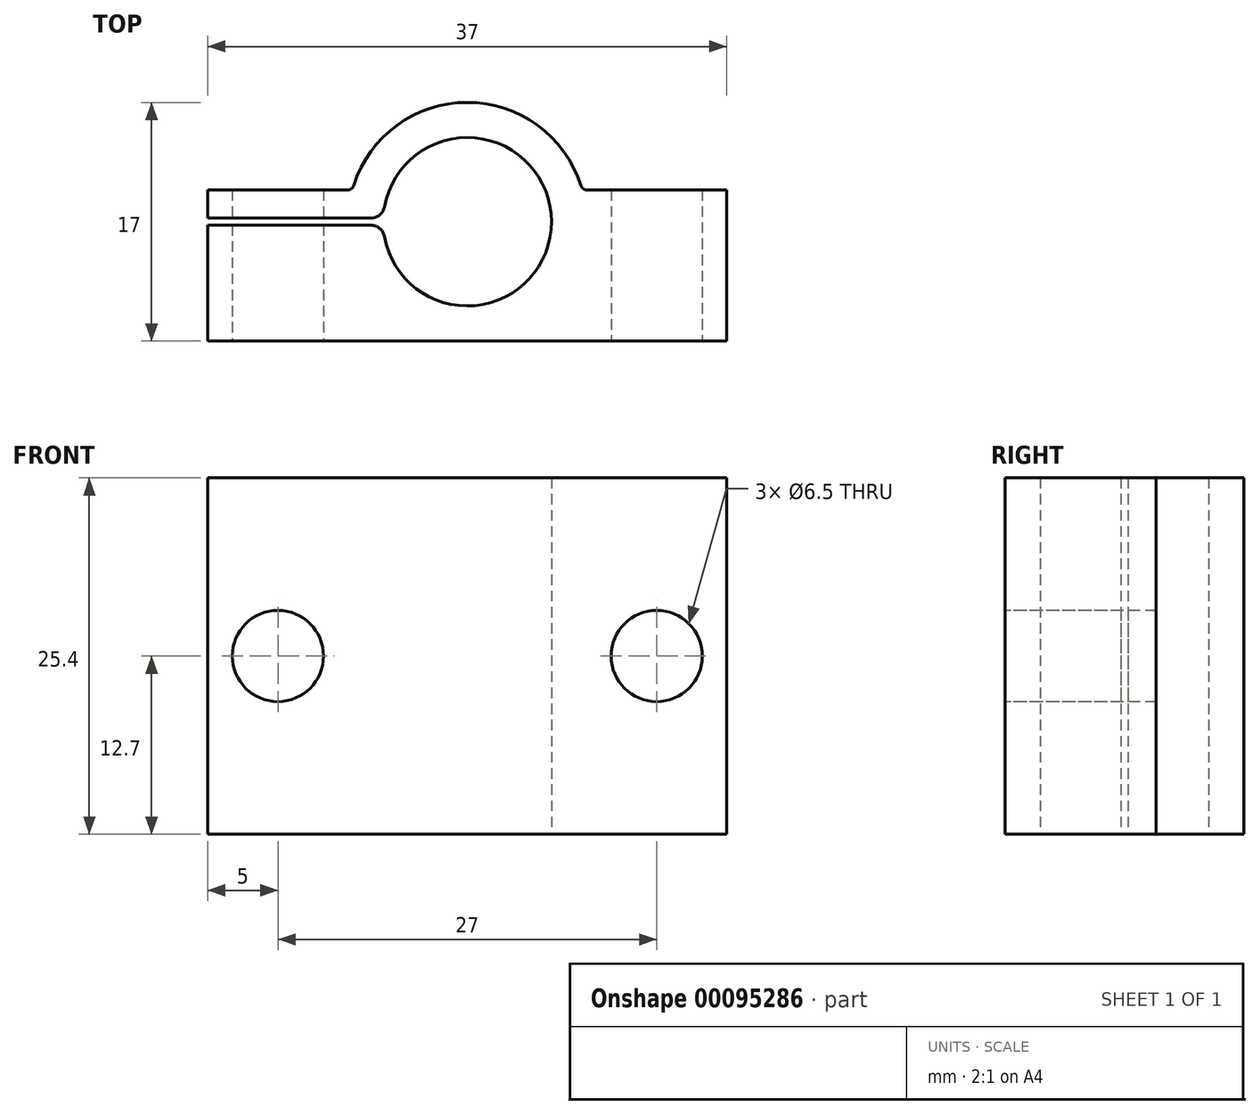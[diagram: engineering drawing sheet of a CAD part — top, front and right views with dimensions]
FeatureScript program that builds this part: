
annotation { "Feature Type Name" : "Feature", "Feature Type Description" : "" }
export const myFeature = defineFeature(function(context is Context, id is Id, definition is map)
    precondition{}
    {
        {
            var Q0;
            Q0=qCreatedBy(makeId("Top.planeOp"),FACE);
            var sketch = newSketch(context, id + "F0", { "sketchPlane" : qUnion([Q0])});
            skLineSegment(sketch, "E0.top", {"start": v(-18.5, -8.5) * mm, "end": v(18.5, -8.5) * mm});
            skPoint(sketch, "E1", {"position": v(0, -8.5) * mm});
            skArc(sketch, "E2", {"start": v(8.2, 2.25) * mm, "mid": v(0, 8.5) * mm, "end": v(-8.2, 2.25) * mm});
            skLineSegment(sketch, "E3.left", {"start": v(-18.5, -8.5) * mm, "end": v(-18.5, -0.25) * mm});
            skLineSegment(sketch, "E3.right", {"start": v(18.5, -8.5) * mm, "end": v(18.5, 2.25) * mm});
            skArc(sketch, "E4", {"start": v(-6, -0.25) * mm, "mid": v(6, 0) * mm, "end": v(-6, 0.25) * mm});
            skLineSegment(sketch, "E5", {"start": v(-18.5, -0.25) * mm, "end": v(-6, -0.25) * mm});
            skLineSegment(sketch, "E6.top", {"start": v(-18.5, 0.25) * mm, "end": v(-6, 0.25) * mm});
            skLineSegment(sketch, "E7.top", {"start": v(-18.5, 2.25) * mm, "end": v(-8.2, 2.25) * mm});
            skLineSegment(sketch, "E7.left", {"start": v(-18.5, 0.25) * mm, "end": v(-18.5, 2.25) * mm});
            skLineSegment(sketch, "E8", {"start": v(18.5, 2.25) * mm, "end": v(8.2, 2.25) * mm});
            skSolve(sketch);
        }
        {
            var Q0;
            Q0 = qSketchRegion(id + "F0", true);
            extrude(context, id + "F1", {"entities" : qUnion([Q0]), "depth" : 25.4 * mm});
        }
        {
            var Q0;
            Q0=makeQuery(id+"F1.opExtrude","SWEPT_EDGE",EDGE,{"disambiguationData":[OSD([sQuery(id+"F0.wireOp",EDGE,"E4"),sQuery(id+"F0.wireOp",EDGE,"E6.top")])]});
            var Q1;
            Q1=makeQuery(id+"F1.opExtrude","SWEPT_EDGE",EDGE,{"disambiguationData":[OSD([sQuery(id+"F0.wireOp",EDGE,"E4"),sQuery(id+"F0.wireOp",EDGE,"E5")])]});
            fillet(context, id + "F2", {"entities" : qUnion([Q0, Q1]), "radius" : 1 * mm, "tangentPropagation" : true, "allowEdgeOverflow" : false});
        }
        {
            var Q0;
            Q0=makeQuery(id+"F1.opExtrude","SWEPT_EDGE",EDGE,{"disambiguationData":[OSD([sQuery(id+"F0.wireOp",EDGE,"E2"),sQuery(id+"F0.wireOp",EDGE,"E7.top")])]});
            var Q1;
            Q1=makeQuery(id+"F1.opExtrude","SWEPT_EDGE",EDGE,{"disambiguationData":[OSD([sQuery(id+"F0.wireOp",EDGE,"E2"),sQuery(id+"F0.wireOp",EDGE,"E8")])]});
            fillet(context, id + "F3", {"entities" : qUnion([Q0, Q1]), "radius" : 0.5 * mm, "tangentPropagation" : true, "allowEdgeOverflow" : false});
        }
        {
            var Q0;
            Q0=makeQuery(id+"F1.opExtrude","SWEPT_FACE",FACE,{"disambiguationData":[OSD([sQuery(id+"F0.wireOp",EDGE,"E0.top")])]});
            var sketch = newSketch(context, id + "F4", { "sketchPlane" : qUnion([Q0])});
            skLineSegment(sketch, "E9", {"start": v(-23.16, 12.7) * mm, "end": v(27.84, 12.7) * mm, "construction": true});
            skPoint(sketch, "E9.startSnap0", {"position": v(-18.5, 12.7) * mm});
            skPoint(sketch, "E9.endSnap0", {"position": v(-18.5, 12.7) * mm});
            skCircle(sketch, "E10", {"center": v(-13.5, 12.7) * mm, "radius": 3.25 * mm});
            skCircle(sketch, "E11.MirrorC", {"center": v(13.5, 12.7) * mm, "radius": 3.25 * mm});
            skSolve(sketch);
        }
        {
            var Q0;
            Q0 = qSketchRegion(id + "F4", true);
            extrude(context, id + "F5", {"entities" : qUnion([Q0]), "operationType" : NewBodyOperationType.REMOVE, "endBound" : BoundingType.THROUGH_ALL, "oppositeDirection" : true, "depth" : 25 * mm});
        }
    });
